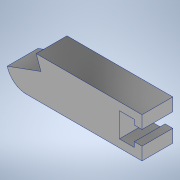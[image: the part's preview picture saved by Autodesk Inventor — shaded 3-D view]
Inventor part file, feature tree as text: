
AUTODESK INVENTOR PART (.ipt)
format: ipt  version: 2022 (Build 260153000, 153)  size: 146,944 bytes
history: native  units: mm
features: extrude x2, sketch x2
ambient origin geometry x8: Origin, YZ Plane, XZ Plane, XY Plane, X Axis, Y Axis, Z Axis, Center Point
bodies: Body1 (feature_tree)
feature tree (4):
  extrude  "Extrusion2"  Depth=5.8mm
  extrude  "Extrusion5"  Depth=3.0mm
  sketch  "Sketch5"  dims[d41=5.8mm d48=44.0mm]
  sketch  "Sketch8"  dims[d56=12.0mm d57=0.0mm d63=45.0mm d67=15.6mm d71=0.0mm d72=36.2mm d80=19.198622mm d81=3.490659mm d82=0.0mm d83=0.0mm d84=3.490659mm d85=5.6mm d86=9.5mm d87=3.0mm d88=14.0mm]
